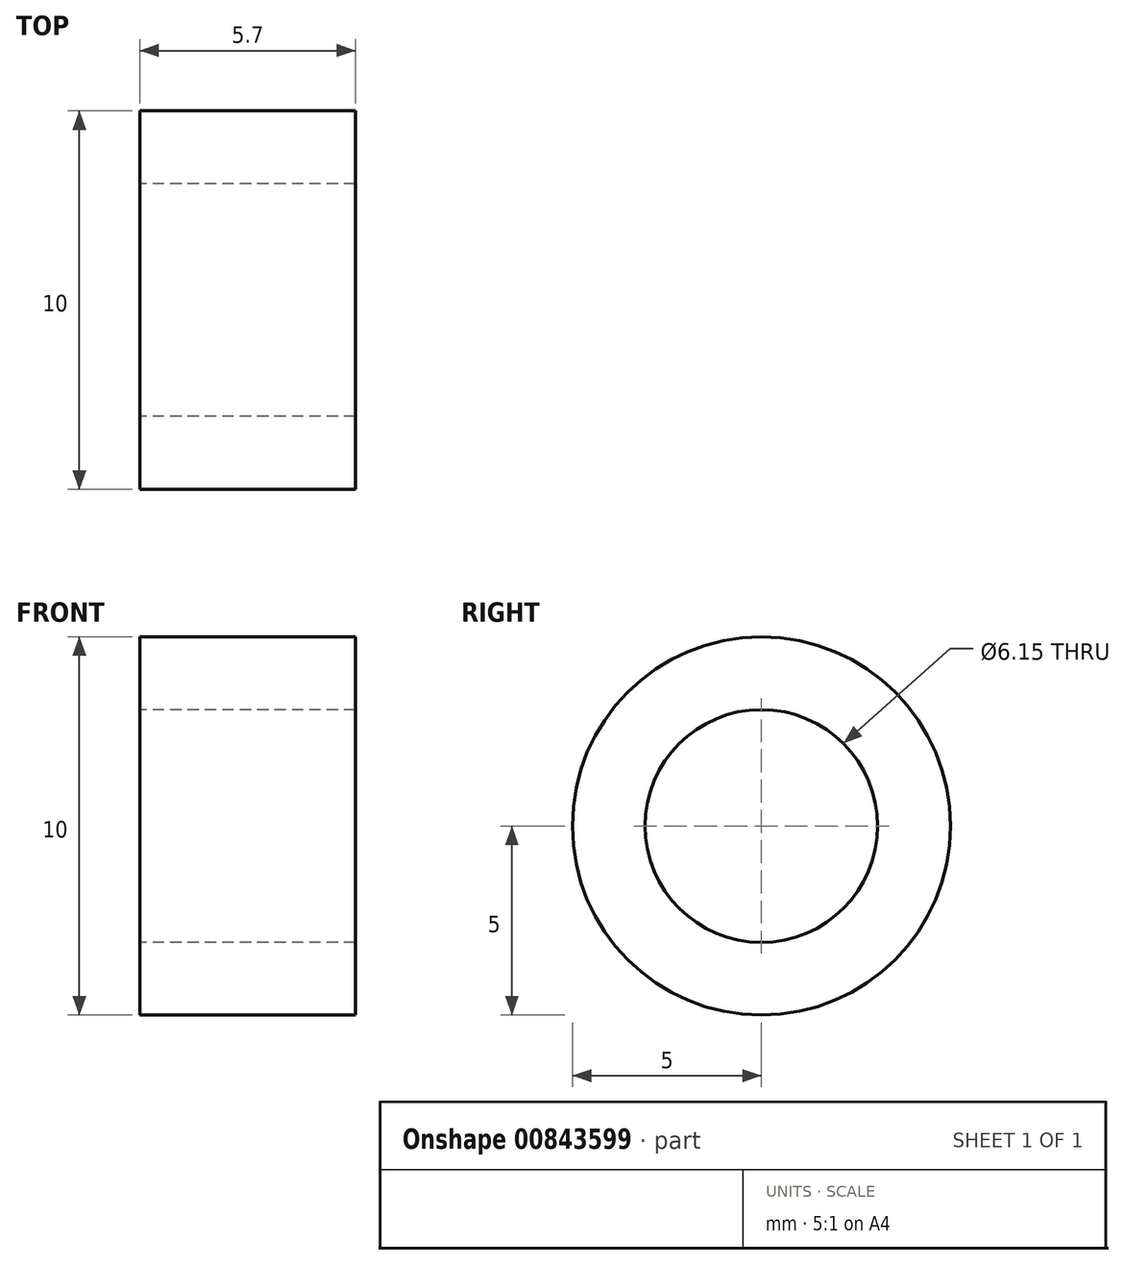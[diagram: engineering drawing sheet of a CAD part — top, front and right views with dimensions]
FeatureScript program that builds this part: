
annotation { "Feature Type Name" : "Feature", "Feature Type Description" : "" }
export const myFeature = defineFeature(function(context is Context, id is Id, definition is map)
    precondition{}
    {
        {
            var Q0;
            Q0=qCreatedBy(makeId("Right.planeOp"),FACE);
            var sketch = newSketch(context, id + "F0", { "sketchPlane" : qUnion([Q0])});
            skCircle(sketch, "E0", {"center": v(0, 0) * mm, "radius": 3.08 * mm});
            skCircle(sketch, "E1", {"center": v(0, 0) * mm, "radius": 5 * mm});
            skSolve(sketch);
        }
        {
            var Q0;
            Q0=makeQuery(id+"F0.imprint","IMPRINT",FACE,{"disambiguationData":[TD([[makeQuery(id+"F0.imprint","IMPRINT",EDGE,{"derivedFrom":sQuery(id+"F0.wireOp",EDGE,"E0")}),-1.0]])]});
            extrude(context, id + "F1", {"entities" : qUnion([Q0]), "depth" : 5.7 * mm, "offsetDistance" : 25 * mm});
        }
    });
